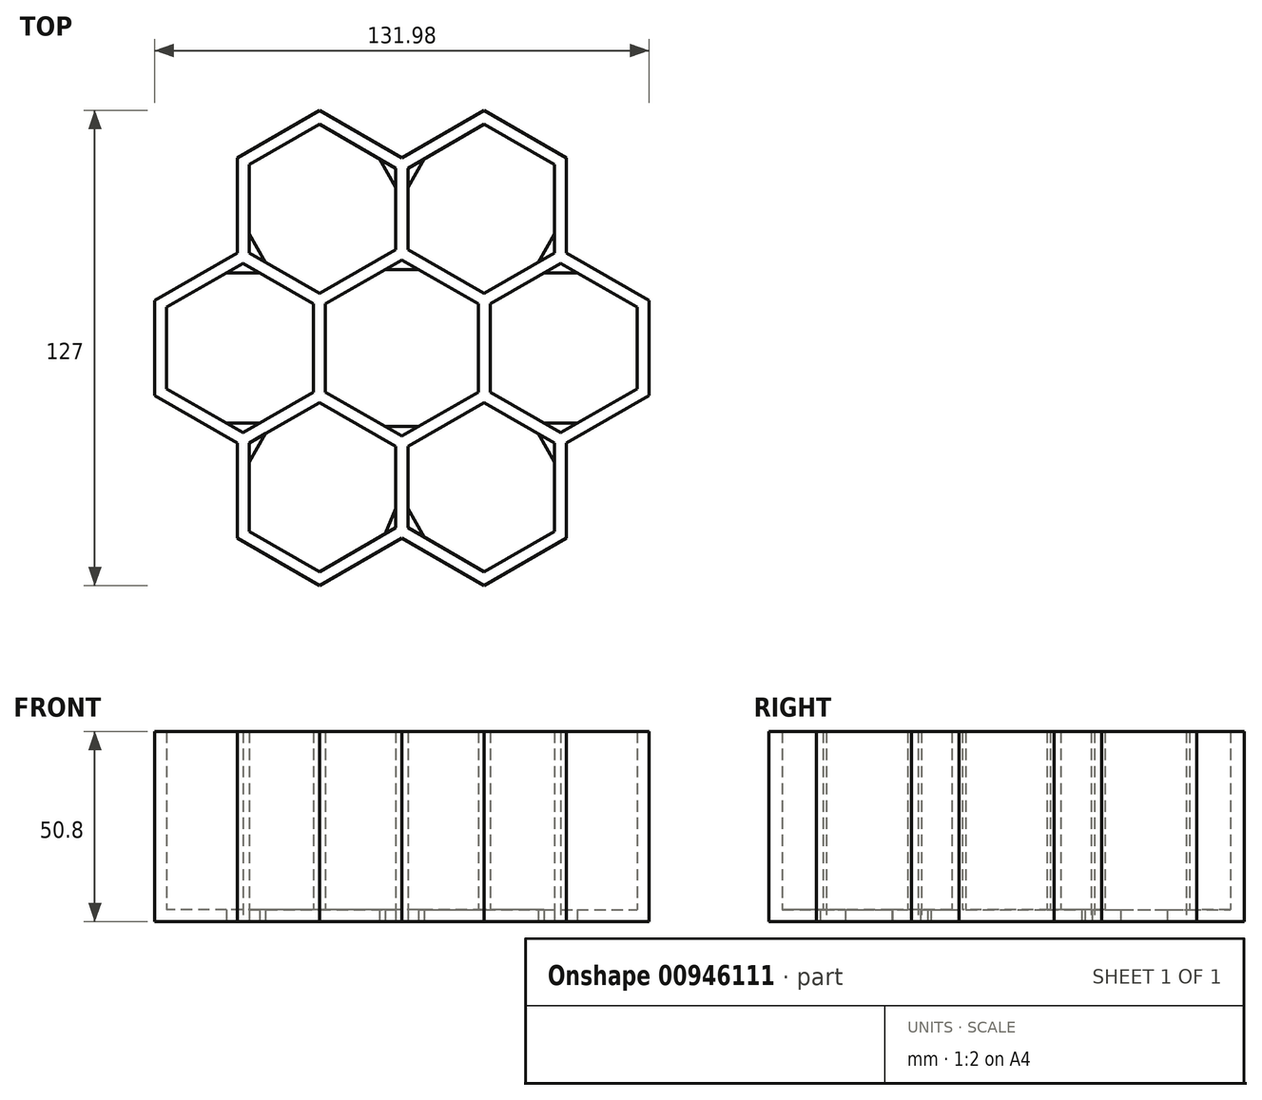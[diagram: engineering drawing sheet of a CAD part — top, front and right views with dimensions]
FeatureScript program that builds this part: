
annotation { "Feature Type Name" : "Feature", "Feature Type Description" : "" }
export const myFeature = defineFeature(function(context is Context, id is Id, definition is map)
    precondition{}
    {
        {
            var Q0;
            Q0=qCreatedBy(makeId("Top.planeOp"),FACE);
            var sketch = newSketch(context, id + "F0", { "sketchPlane" : qUnion([Q0])});
            skCircle(sketch, "E0.cCircle", {"center": v(0, 0) * mm, "radius": 25.4 * mm, "construction": true});
            skLineSegment(sketch, "E0.0", {"start": v(0, 25.4) * mm, "end": v(22, 12.7) * mm});
            skLineSegment(sketch, "E0.1", {"start": v(22, 12.7) * mm, "end": v(22, -12.7) * mm});
            skLineSegment(sketch, "E0.2", {"start": v(22, -12.7) * mm, "end": v(0, -25.4) * mm});
            skLineSegment(sketch, "E0.3", {"start": v(0, -25.4) * mm, "end": v(-22, -12.7) * mm});
            skLineSegment(sketch, "E0.4", {"start": v(-22, -12.7) * mm, "end": v(-22, 12.7) * mm});
            skLineSegment(sketch, "E0.5", {"start": v(-22, 12.7) * mm, "end": v(0, 25.4) * mm});
            skLineSegment(sketch, "E1.MirrorCS", {"start": v(-22, 12.7) * mm, "end": v(-44, 25.4) * mm});
            skLineSegment(sketch, "E2.MirrorCS", {"start": v(-44, 25.4) * mm, "end": v(-66, 12.7) * mm});
            skLineSegment(sketch, "E3.MirrorCS", {"start": v(-66, 12.7) * mm, "end": v(-66, -12.7) * mm});
            skLineSegment(sketch, "E4.MirrorCS", {"start": v(-66, -12.7) * mm, "end": v(-44, -25.4) * mm});
            skLineSegment(sketch, "E5.MirrorCS", {"start": v(-44, -25.4) * mm, "end": v(-22, -12.7) * mm});
            skLineSegment(sketch, "E6.MirrorCS", {"start": v(-22, -12.7) * mm, "end": v(-44, -25.4) * mm});
            skLineSegment(sketch, "E7.MirrorCS", {"start": v(-44, -25.4) * mm, "end": v(-44, -50.8) * mm});
            skLineSegment(sketch, "E8.MirrorCS", {"start": v(-44, -50.8) * mm, "end": v(-22, -63.5) * mm});
            skLineSegment(sketch, "E9.MirrorCS", {"start": v(-22, -63.5) * mm, "end": v(0, -50.8) * mm});
            skLineSegment(sketch, "E10.MirrorCS", {"start": v(0, -50.8) * mm, "end": v(0, -25.4) * mm});
            skLineSegment(sketch, "E11.MirrorCS", {"start": v(0, -25.4) * mm, "end": v(0, -50.8) * mm});
            skLineSegment(sketch, "E12.MirrorCS", {"start": v(0, -50.8) * mm, "end": v(22, -63.5) * mm});
            skLineSegment(sketch, "E13.MirrorCS", {"start": v(22, -63.5) * mm, "end": v(44, -50.8) * mm});
            skLineSegment(sketch, "E14.MirrorCS", {"start": v(44, -50.8) * mm, "end": v(44, -25.4) * mm});
            skLineSegment(sketch, "E15.MirrorCS", {"start": v(44, -25.4) * mm, "end": v(22, -12.7) * mm});
            skLineSegment(sketch, "E16.MirrorCS", {"start": v(-44, 25.4) * mm, "end": v(-22, 12.7) * mm});
            skLineSegment(sketch, "E17.MirrorCS", {"start": v(-44, 50.8) * mm, "end": v(-44, 25.4) * mm});
            skLineSegment(sketch, "E18.MirrorCS", {"start": v(-22, 63.5) * mm, "end": v(-44, 50.8) * mm});
            skLineSegment(sketch, "E19.MirrorCS", {"start": v(0, 50.8) * mm, "end": v(-22, 63.5) * mm});
            skLineSegment(sketch, "E20.MirrorCS", {"start": v(0, 25.4) * mm, "end": v(0, 50.8) * mm});
            skLineSegment(sketch, "E21.MirrorCS", {"start": v(0, 50.8) * mm, "end": v(0, 25.4) * mm});
            skLineSegment(sketch, "E22.MirrorCS", {"start": v(22, 63.5) * mm, "end": v(0, 50.8) * mm});
            skLineSegment(sketch, "E23.MirrorCS", {"start": v(44, 50.8) * mm, "end": v(22, 63.5) * mm});
            skLineSegment(sketch, "E24.MirrorCS", {"start": v(44, 25.4) * mm, "end": v(44, 50.8) * mm});
            skLineSegment(sketch, "E25.MirrorCS", {"start": v(22, 12.7) * mm, "end": v(44, 25.4) * mm});
            skLineSegment(sketch, "E26.MirrorCS", {"start": v(44, 25.4) * mm, "end": v(22, 12.7) * mm});
            skLineSegment(sketch, "E27.MirrorCS", {"start": v(66, 12.7) * mm, "end": v(44, 25.4) * mm});
            skLineSegment(sketch, "E28.MirrorCS", {"start": v(66, -12.7) * mm, "end": v(66, 12.7) * mm});
            skLineSegment(sketch, "E29.MirrorCS", {"start": v(44, -25.4) * mm, "end": v(66, -12.7) * mm});
            skLineSegment(sketch, "E30.0", {"start": v(0, 47.13) * mm, "end": v(-22, 59.83) * mm});
            skLineSegment(sketch, "E30.1", {"start": v(22, 59.83) * mm, "end": v(0, 47.13) * mm});
            skLineSegment(sketch, "E30.2", {"start": v(40.82, 48.97) * mm, "end": v(22, 59.83) * mm});
            skLineSegment(sketch, "E30.3", {"start": v(40.82, 23.57) * mm, "end": v(40.82, 48.97) * mm});
            skLineSegment(sketch, "E30.4", {"start": v(62.82, 10.87) * mm, "end": v(40.82, 23.57) * mm});
            skLineSegment(sketch, "E30.5", {"start": v(-22, 59.83) * mm, "end": v(-40.82, 48.97) * mm});
            skLineSegment(sketch, "E30.6", {"start": v(62.82, -10.87) * mm, "end": v(62.82, 10.87) * mm});
            skLineSegment(sketch, "E30.7", {"start": v(40.82, -23.57) * mm, "end": v(62.82, -10.87) * mm});
            skLineSegment(sketch, "E30.8", {"start": v(-62.82, -10.87) * mm, "end": v(-40.82, -23.57) * mm});
            skLineSegment(sketch, "E30.9", {"start": v(-62.82, 10.87) * mm, "end": v(-62.82, -10.87) * mm});
            skLineSegment(sketch, "E30.10", {"start": v(-40.82, 23.57) * mm, "end": v(-62.82, 10.87) * mm});
            skLineSegment(sketch, "E30.11", {"start": v(-40.82, 48.97) * mm, "end": v(-40.82, 23.57) * mm});
            skLineSegment(sketch, "E30.12", {"start": v(-40.82, -23.57) * mm, "end": v(-40.82, -48.97) * mm});
            skLineSegment(sketch, "E30.13", {"start": v(-40.82, -48.97) * mm, "end": v(-22, -59.83) * mm});
            skLineSegment(sketch, "E30.14", {"start": v(-22, -59.83) * mm, "end": v(0, -47.13) * mm});
            skLineSegment(sketch, "E30.15", {"start": v(0, -47.13) * mm, "end": v(22, -59.83) * mm});
            skLineSegment(sketch, "E30.16", {"start": v(22, -59.83) * mm, "end": v(40.82, -48.97) * mm});
            skLineSegment(sketch, "E30.17", {"start": v(40.82, -48.97) * mm, "end": v(40.82, -23.57) * mm});
            skLineSegment(sketch, "E31.0", {"start": v(1.6, 26.32) * mm, "end": v(1.6, 50.8) * mm});
            skLineSegment(sketch, "E31.1", {"start": v(1.6, 26.32) * mm, "end": v(22, 14.55) * mm});
            skLineSegment(sketch, "E31.2", {"start": v(43.2, 26.79) * mm, "end": v(22, 14.55) * mm});
            skLineSegment(sketch, "E32.0", {"start": v(-22, 14.55) * mm, "end": v(-43.2, 26.79) * mm});
            skLineSegment(sketch, "E32.1", {"start": v(-22, 14.55) * mm, "end": v(-1.6, 26.32) * mm});
            skLineSegment(sketch, "E32.2", {"start": v(-1.6, 26.32) * mm, "end": v(-1.6, 50.8) * mm});
            skLineSegment(sketch, "E33.0", {"start": v(-23.6, 11.78) * mm, "end": v(-44.8, 24.01) * mm});
            skLineSegment(sketch, "E33.1", {"start": v(-23.6, -11.78) * mm, "end": v(-23.6, 11.78) * mm});
            skLineSegment(sketch, "E33.2", {"start": v(-23.6, -11.78) * mm, "end": v(-44.8, -24.01) * mm});
            skLineSegment(sketch, "E34.0", {"start": v(-22, -14.55) * mm, "end": v(-43.2, -26.79) * mm});
            skLineSegment(sketch, "E34.1", {"start": v(-1.6, -26.32) * mm, "end": v(-22, -14.55) * mm});
            skLineSegment(sketch, "E34.2", {"start": v(-1.6, -50.6) * mm, "end": v(-1.6, -26.32) * mm});
            skLineSegment(sketch, "E35.0", {"start": v(43.2, -26.79) * mm, "end": v(22, -14.55) * mm});
            skLineSegment(sketch, "E35.1", {"start": v(22, -14.55) * mm, "end": v(1.6, -26.32) * mm});
            skLineSegment(sketch, "E35.2", {"start": v(1.6, -50.8) * mm, "end": v(1.6, -26.32) * mm});
            skLineSegment(sketch, "E36.0", {"start": v(44.8, -24.01) * mm, "end": v(23.6, -11.78) * mm});
            skLineSegment(sketch, "E36.1", {"start": v(23.6, 11.78) * mm, "end": v(23.6, -11.78) * mm});
            skLineSegment(sketch, "E36.2", {"start": v(44.8, 24.01) * mm, "end": v(23.6, 11.78) * mm});
            skLineSegment(sketch, "E37.0", {"start": v(-20.4, -11.78) * mm, "end": v(-20.4, 11.78) * mm});
            skLineSegment(sketch, "E37.1", {"start": v(0, 23.55) * mm, "end": v(20.4, 11.78) * mm});
            skLineSegment(sketch, "E37.2", {"start": v(20.4, 11.78) * mm, "end": v(20.4, -11.78) * mm});
            skLineSegment(sketch, "E37.3", {"start": v(-20.4, 11.78) * mm, "end": v(0, 23.55) * mm});
            skLineSegment(sketch, "E37.4", {"start": v(20.4, -11.78) * mm, "end": v(0, -23.55) * mm});
            skLineSegment(sketch, "E37.5", {"start": v(0, -23.55) * mm, "end": v(-20.4, -11.78) * mm});
            skLineSegment(sketch, "E38", {"start": v(-62.82, -10.87) * mm, "end": v(-42.42, -22.64) * mm});
            skLineSegment(sketch, "E39", {"start": v(-42.42, -22.64) * mm, "end": v(-46.82, -20.1) * mm});
            skLineSegment(sketch, "E40", {"start": v(-42.42, -22.64) * mm, "end": v(-38.02, -20.1) * mm});
            skLineSegment(sketch, "E41", {"start": v(-38.02, -20.1) * mm, "end": v(-46.82, -20.1) * mm});
            skLineSegment(sketch, "E42", {"start": v(-62.82, 10.87) * mm, "end": v(-42.42, 22.64) * mm});
            skLineSegment(sketch, "E43", {"start": v(-42.42, 22.64) * mm, "end": v(-46.82, 20.1) * mm});
            skLineSegment(sketch, "E44", {"start": v(-42.42, 22.64) * mm, "end": v(-38.02, 20.1) * mm});
            skLineSegment(sketch, "E45", {"start": v(-38.02, 20.1) * mm, "end": v(-46.82, 20.1) * mm});
            skLineSegment(sketch, "E46", {"start": v(-40.82, 48.97) * mm, "end": v(-40.82, 25.41) * mm});
            skLineSegment(sketch, "E47", {"start": v(-40.82, 25.41) * mm, "end": v(-40.82, 30.5) * mm});
            skLineSegment(sketch, "E48", {"start": v(-40.82, 25.41) * mm, "end": v(-36.42, 22.87) * mm});
            skLineSegment(sketch, "E49", {"start": v(-36.42, 22.87) * mm, "end": v(-40.82, 30.5) * mm});
            skLineSegment(sketch, "E50", {"start": v(-22, 59.83) * mm, "end": v(-1.6, 48.06) * mm});
            skLineSegment(sketch, "E51", {"start": v(-1.6, 48.06) * mm, "end": v(-6, 50.6) * mm});
            skLineSegment(sketch, "E52", {"start": v(-1.6, 48.06) * mm, "end": v(-1.6, 42.98) * mm});
            skLineSegment(sketch, "E53", {"start": v(-1.6, 42.98) * mm, "end": v(-6, 50.6) * mm});
            skLineSegment(sketch, "E54", {"start": v(1.6, 26.32) * mm, "end": v(1.6, 48.06) * mm});
            skLineSegment(sketch, "E55", {"start": v(1.6, 48.06) * mm, "end": v(1.6, 42.98) * mm});
            skLineSegment(sketch, "E56", {"start": v(1.6, 48.06) * mm, "end": v(6, 50.6) * mm});
            skLineSegment(sketch, "E57", {"start": v(6, 50.6) * mm, "end": v(1.6, 42.98) * mm});
            skLineSegment(sketch, "E58", {"start": v(40.82, 48.97) * mm, "end": v(40.82, 23.57) * mm});
            skLineSegment(sketch, "E59", {"start": v(40.82, 23.57) * mm, "end": v(40.82, 28.65) * mm});
            skLineSegment(sketch, "E60", {"start": v(40.82, 23.57) * mm, "end": v(36.42, 21.03) * mm});
            skLineSegment(sketch, "E61", {"start": v(23.6, 11.78) * mm, "end": v(42.42, 22.64) * mm});
            skLineSegment(sketch, "E62", {"start": v(42.42, 22.64) * mm, "end": v(38.02, 20.1) * mm});
            skLineSegment(sketch, "E63", {"start": v(42.42, 22.64) * mm, "end": v(46.82, 20.1) * mm});
            skLineSegment(sketch, "E64", {"start": v(46.82, 20.1) * mm, "end": v(38.02, 20.1) * mm});
            skLineSegment(sketch, "E65", {"start": v(40.82, 48.97) * mm, "end": v(40.82, 25.41) * mm});
            skLineSegment(sketch, "E66", {"start": v(40.82, 25.41) * mm, "end": v(40.82, 30.5) * mm});
            skLineSegment(sketch, "E67", {"start": v(40.82, 25.41) * mm, "end": v(36.42, 22.87) * mm});
            skLineSegment(sketch, "E68", {"start": v(36.42, 22.87) * mm, "end": v(40.82, 30.5) * mm});
            skLineSegment(sketch, "E69", {"start": v(62.82, -10.87) * mm, "end": v(42.42, -22.64) * mm});
            skLineSegment(sketch, "E70", {"start": v(42.42, -22.64) * mm, "end": v(46.82, -20.1) * mm});
            skLineSegment(sketch, "E71", {"start": v(42.42, -22.64) * mm, "end": v(38.02, -20.1) * mm});
            skLineSegment(sketch, "E72", {"start": v(38.02, -20.1) * mm, "end": v(46.82, -20.1) * mm});
            skLineSegment(sketch, "E73", {"start": v(40.82, -48.97) * mm, "end": v(40.82, -25.41) * mm});
            skLineSegment(sketch, "E74", {"start": v(40.82, -25.41) * mm, "end": v(40.82, -30.5) * mm});
            skLineSegment(sketch, "E75", {"start": v(40.82, -25.41) * mm, "end": v(36.42, -22.87) * mm});
            skLineSegment(sketch, "E76", {"start": v(36.42, -22.87) * mm, "end": v(40.82, -30.5) * mm});
            skLineSegment(sketch, "E77", {"start": v(22, -59.83) * mm, "end": v(1.6, -48.06) * mm});
            skLineSegment(sketch, "E78", {"start": v(1.6, -48.06) * mm, "end": v(6, -50.6) * mm});
            skLineSegment(sketch, "E79", {"start": v(1.6, -48.06) * mm, "end": v(1.6, -42.98) * mm});
            skLineSegment(sketch, "E80", {"start": v(1.6, -42.98) * mm, "end": v(6, -50.6) * mm});
            skLineSegment(sketch, "E81", {"start": v(-1.6, -26.32) * mm, "end": v(-1.6, -48.06) * mm});
            skLineSegment(sketch, "E82", {"start": v(-1.6, -48.06) * mm, "end": v(-1.6, -42.98) * mm});
            skLineSegment(sketch, "E83", {"start": v(0, -47.13) * mm, "end": v(-4.4, -49.67) * mm});
            skLineSegment(sketch, "E84", {"start": v(-4.4, -49.67) * mm, "end": v(-1.6, -42.98) * mm});
            skLineSegment(sketch, "E85", {"start": v(-40.82, -48.97) * mm, "end": v(-40.82, -25.4) * mm});
            skLineSegment(sketch, "E86", {"start": v(-40.82, -25.4) * mm, "end": v(-40.82, -30.48) * mm});
            skLineSegment(sketch, "E87", {"start": v(-40.82, -25.4) * mm, "end": v(-36.41, -22.87) * mm});
            skLineSegment(sketch, "E88", {"start": v(-36.41, -22.87) * mm, "end": v(-40.82, -30.48) * mm});
            skLineSegment(sketch, "E89", {"start": v(0, -23.55) * mm, "end": v(-4.4, -21.01) * mm});
            skLineSegment(sketch, "E90", {"start": v(0, -23.55) * mm, "end": v(4.4, -21.01) * mm});
            skLineSegment(sketch, "E91", {"start": v(4.4, -21.01) * mm, "end": v(-4.4, -21.01) * mm});
            skLineSegment(sketch, "E92", {"start": v(0, 23.55) * mm, "end": v(4.4, 21.01) * mm});
            skLineSegment(sketch, "E93", {"start": v(0, 23.55) * mm, "end": v(-4.4, 21.01) * mm});
            skLineSegment(sketch, "E94", {"start": v(-4.4, 21.01) * mm, "end": v(4.4, 21.01) * mm});
            skLineSegment(sketch, "E95", {"start": v(0, -25.4) * mm, "end": v(1.6, -26.32) * mm});
            skLineSegment(sketch, "E96", {"start": v(22, -12.7) * mm, "end": v(22, -14.55) * mm});
            skLineSegment(sketch, "E97", {"start": v(-22, 12.7) * mm, "end": v(-20.4, 11.78) * mm});
            skLineSegment(sketch, "E98", {"start": v(0, 25.4) * mm, "end": v(0, 23.55) * mm});
            skLineSegment(sketch, "E99", {"start": v(0, -23.55) * mm, "end": v(0, -25.4) * mm});
            skLineSegment(sketch, "E100", {"start": v(20.4, -11.78) * mm, "end": v(22, -12.7) * mm});
            skSolve(sketch);
        }
        {
            var Q0;
            {var subQ9=sQuery(id+"F0.wireOp",EDGE,"E2.MirrorCS");Q0=makeQuery(id+"F0.imprint","IMPRINT",FACE,{"disambiguationData":[TD([[makeQuery(id+"F0.imprint","IMPRINT",EDGE,{"derivedFrom":subQ9}),1.0]])]});}
            var Q1;
            {var subQ9=sQuery(id+"F0.wireOp",EDGE,"E17.MirrorCS");Q1=makeQuery(id+"F0.imprint","IMPRINT",FACE,{"disambiguationData":[TD([[makeQuery(id+"F0.imprint","IMPRINT",EDGE,{"derivedFrom":subQ9}),1.0]])]});}
            var Q2;
            {var subQ10=sQuery(id+"F0.wireOp",EDGE,"E22.MirrorCS");Q2=makeQuery(id+"F0.imprint","IMPRINT",FACE,{"disambiguationData":[TD([[makeQuery(id+"F0.imprint","IMPRINT",EDGE,{"derivedFrom":subQ10}),1.0]])]});}
            var Q3;
            {var subQ11=sQuery(id+"F0.wireOp",EDGE,"E27.MirrorCS");Q3=makeQuery(id+"F0.imprint","IMPRINT",FACE,{"disambiguationData":[TD([[makeQuery(id+"F0.imprint","IMPRINT",EDGE,{"derivedFrom":subQ11}),1.0]])]});}
            var Q4;
            {var subQ10=sQuery(id+"F0.wireOp",EDGE,"E12.MirrorCS");Q4=makeQuery(id+"F0.imprint","IMPRINT",FACE,{"disambiguationData":[TD([[makeQuery(id+"F0.imprint","IMPRINT",EDGE,{"derivedFrom":subQ10}),1.0]])]});}
            var Q5;
            {var subQ8=sQuery(id+"F0.wireOp",EDGE,"E7.MirrorCS");Q5=makeQuery(id+"F0.imprint","IMPRINT",FACE,{"disambiguationData":[TD([[makeQuery(id+"F0.imprint","IMPRINT",EDGE,{"derivedFrom":subQ8}),1.0]])]});}
            var Q6;
            {var subQ8=sQuery(id+"F0.wireOp",EDGE,"E0.4");Q6=makeQuery(id+"F0.imprint","IMPRINT",FACE,{"disambiguationData":[TD([[makeQuery(id+"F0.imprint","IMPRINT",EDGE,{"derivedFrom":subQ8}),1.0]])]});}
            var Q7;
            {var subQ6=sQuery(id+"F0.wireOp",EDGE,"E0.5");Q7=makeQuery(id+"F0.imprint","IMPRINT",FACE,{"disambiguationData":[TD([[makeQuery(id+"F0.imprint","IMPRINT",EDGE,{"derivedFrom":subQ6}),1.0]])]});}
            var Q8;
            Q8=makeQuery(id+"F0.imprint","IMPRINT",FACE,{"disambiguationData":[TD([[makeQuery(id+"F0.imprint","IMPRINT",EDGE,{"derivedFrom":sQuery(id+"F0.wireOp",EDGE,"E0.0")}),-1.0]])]});
            var Q9;
            {var subQ1=sQuery(id+"F0.wireOp",EDGE,"E0.3");Q9=makeQuery(id+"F0.imprint","IMPRINT",FACE,{"disambiguationData":[TD([[makeQuery(id+"F0.imprint","IMPRINT",EDGE,{"derivedFrom":subQ1}),1.0]])]});}
            var Q10;
            Q10=makeQuery(id+"F0.imprint","IMPRINT",FACE,{"disambiguationData":[TD([[makeQuery(id+"F0.imprint","IMPRINT",EDGE,{"derivedFrom":sQuery(id+"F0.wireOp",EDGE,"E0.2")}),1.0]])]});
            var Q11;
            {var subQ11=sQuery(id+"F0.wireOp",EDGE,"E0.0");Q11=makeQuery(id+"F0.imprint","IMPRINT",FACE,{"disambiguationData":[TD([[makeQuery(id+"F0.imprint","IMPRINT",EDGE,{"derivedFrom":subQ11}),1.0]])]});}
            var Q12;
            {var subQ13=sQuery(id+"F0.wireOp",EDGE,"E0.1");Q12=makeQuery(id+"F0.imprint","IMPRINT",FACE,{"disambiguationData":[TD([[makeQuery(id+"F0.imprint","IMPRINT",EDGE,{"derivedFrom":subQ13}),1.0]])]});}
            var Q13;
            Q13=makeQuery(id+"F0.imprint","IMPRINT",FACE,{"disambiguationData":[TD([[makeQuery(id+"F0.imprint","IMPRINT",EDGE,{"derivedFrom":sQuery(id+"F0.wireOp",EDGE,"E0.5")}),-1.0]])]});
            var Q14;
            {var subQ6=sQuery(id+"F0.wireOp",EDGE,"E96");Q14=makeQuery(id+"F0.imprint","IMPRINT",FACE,{"disambiguationData":[TD([[makeQuery(id+"F0.imprint","IMPRINT",EDGE,{"derivedFrom":subQ6}),1.0]])]});}
            var Q15;
            {var subQ4=sQuery(id+"F0.wireOp",EDGE,"E95");Q15=makeQuery(id+"F0.imprint","IMPRINT",FACE,{"disambiguationData":[TD([[makeQuery(id+"F0.imprint","IMPRINT",EDGE,{"derivedFrom":subQ4}),-1.0]])]});}
            var Q16;
            Q16=makeQuery(id+"F0.imprint","IMPRINT",FACE,{"disambiguationData":[TD([[makeQuery(id+"F0.imprint","IMPRINT",EDGE,{"derivedFrom":sQuery(id+"F0.wireOp",EDGE,"E0.3")}),-1.0]])]});
            var Q17;
            Q17=makeQuery(id+"F0.imprint","IMPRINT",FACE,{"disambiguationData":[TD([[makeQuery(id+"F0.imprint","IMPRINT",EDGE,{"derivedFrom":sQuery(id+"F0.wireOp",EDGE,"E0.2")}),-1.0]])]});
            extrude(context, id + "F1", {"entities" : qUnion([Q0, Q1, Q2, Q3, Q4, Q5, Q6, Q7, Q8, Q9, Q10, Q11, Q12, Q13, Q14, Q15, Q16, Q17]), "depth" : 50.8 * mm, "offsetDistance" : 25.4 * mm});
        }
        {
            var Q0;
            {var subQ1=sQuery(id+"F0.wireOp",EDGE,"E30.5");Q0=makeQuery(id+"F0.imprint","IMPRINT",FACE,{"disambiguationData":[TD([[makeQuery(id+"F0.imprint","IMPRINT",EDGE,{"derivedFrom":subQ1}),1.0]])]});}
            var Q1;
            {var subQ1=sQuery(id+"F0.wireOp",EDGE,"E30.9");Q1=makeQuery(id+"F0.imprint","IMPRINT",FACE,{"disambiguationData":[TD([[makeQuery(id+"F0.imprint","IMPRINT",EDGE,{"derivedFrom":subQ1}),1.0]])]});}
            var Q2;
            {var subQ1=sQuery(id+"F0.wireOp",EDGE,"E37.0");Q2=makeQuery(id+"F0.imprint","IMPRINT",FACE,{"disambiguationData":[TD([[makeQuery(id+"F0.imprint","IMPRINT",EDGE,{"derivedFrom":subQ1}),-1.0]])]});}
            var Q3;
            {var subQ4=sQuery(id+"F0.wireOp",EDGE,"E30.2");Q3=makeQuery(id+"F0.imprint","IMPRINT",FACE,{"disambiguationData":[TD([[makeQuery(id+"F0.imprint","IMPRINT",EDGE,{"derivedFrom":subQ4}),1.0]])]});}
            var Q4;
            {var subQ3=sQuery(id+"F0.wireOp",EDGE,"E30.6");Q4=makeQuery(id+"F0.imprint","IMPRINT",FACE,{"disambiguationData":[TD([[makeQuery(id+"F0.imprint","IMPRINT",EDGE,{"derivedFrom":subQ3}),1.0]])]});}
            var Q5;
            {var subQ4=sQuery(id+"F0.wireOp",EDGE,"E30.16");Q5=makeQuery(id+"F0.imprint","IMPRINT",FACE,{"disambiguationData":[TD([[makeQuery(id+"F0.imprint","IMPRINT",EDGE,{"derivedFrom":subQ4}),1.0]])]});}
            var Q6;
            {var subQ0=sQuery(id+"F0.wireOp",EDGE,"E30.13");Q6=makeQuery(id+"F0.imprint","IMPRINT",FACE,{"disambiguationData":[TD([[makeQuery(id+"F0.imprint","IMPRINT",EDGE,{"derivedFrom":subQ0}),1.0]])]});}
            var Q7;
            Q7=makeQuery(id+"F0.imprint","IMPRINT",FACE,{"disambiguationData":[TD([[makeQuery(id+"F0.imprint","IMPRINT",EDGE,{"derivedFrom":sQuery(id+"F0.wireOp",EDGE,"E0.5")}),-1.0]])]});
            extrude(context, id + "F2", {"entities" : qUnion([Q0, Q1, Q2, Q3, Q4, Q5, Q6, Q7]), "operationType" : NewBodyOperationType.ADD, "depth" : 3.17 * mm, "offsetDistance" : 25.4 * mm});
        }
    });
